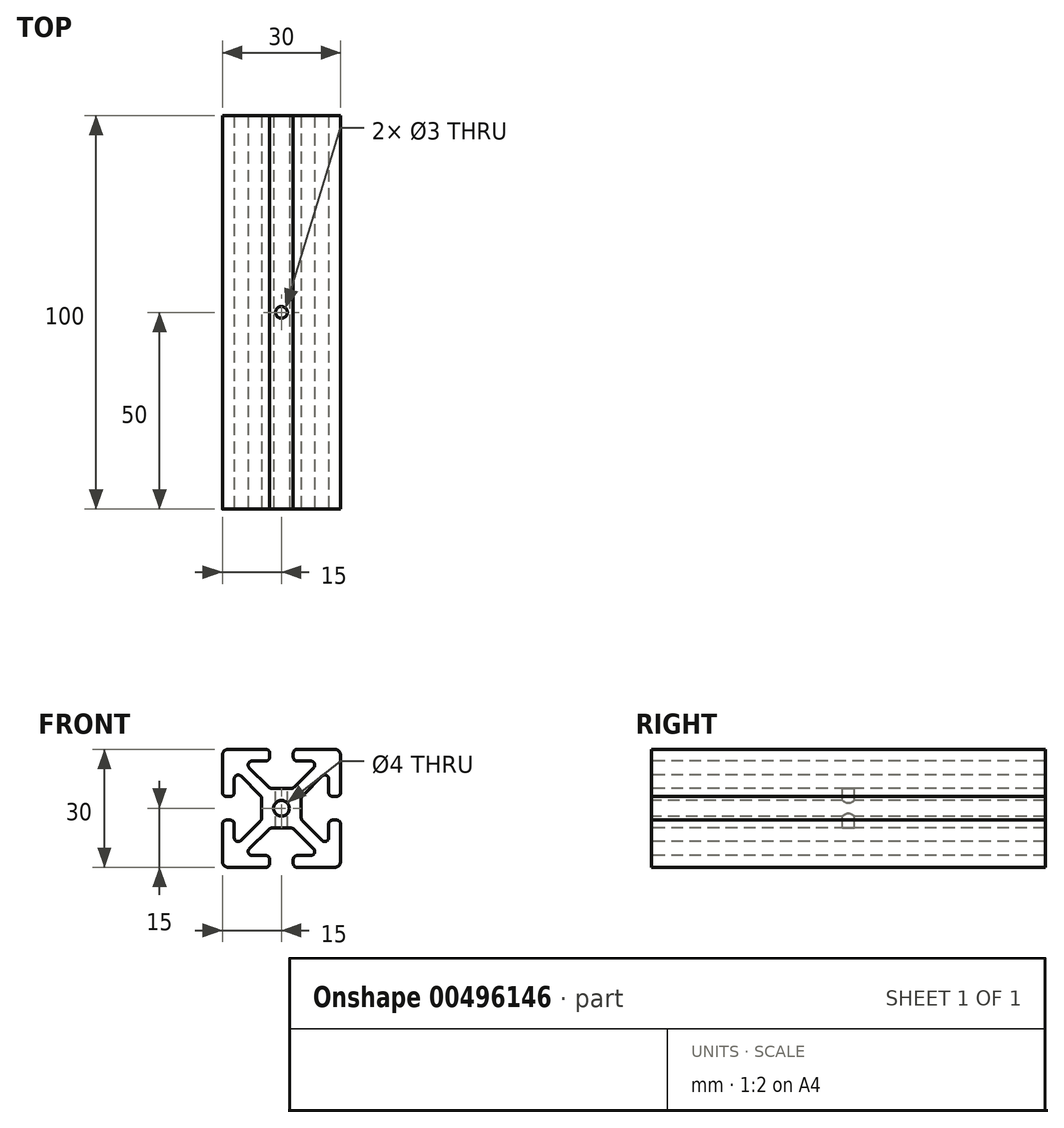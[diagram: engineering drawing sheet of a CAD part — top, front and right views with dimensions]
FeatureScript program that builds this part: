
annotation { "Feature Type Name" : "Feature", "Feature Type Description" : "" }
export const myFeature = defineFeature(function(context is Context, id is Id, definition is map)
    precondition{}
    {
        {
            var Q0;
            Q0=qCreatedBy(makeId("Front.planeOp"),FACE);
            var sketch = newSketch(context, id + "F0", { "sketchPlane" : qUnion([Q0])});
            skLineSegment(sketch, "E0.bottom", {"start": v(13.5, 15) * mm, "end": v(4, 15) * mm});
            skLineSegment(sketch, "E0.top", {"start": v(13.5, -15) * mm, "end": v(4, -15) * mm});
            skLineSegment(sketch, "E0.left", {"start": v(15, 13.5) * mm, "end": v(15, 4) * mm});
            skLineSegment(sketch, "E0.right", {"start": v(-15, 13.5) * mm, "end": v(-15, 4) * mm});
            skPoint(sketch, "E0.middle", {"position": v(0, 0) * mm});
            skLineSegment(sketch, "E1.bottom", {"start": v(7.46, 12) * mm, "end": v(4, 12) * mm});
            skLineSegment(sketch, "E1.top", {"start": v(7.46, -12) * mm, "end": v(4, -12) * mm});
            skLineSegment(sketch, "E1.left", {"start": v(12, 7.46) * mm, "end": v(12, 4) * mm});
            skLineSegment(sketch, "E1.right", {"start": v(-12, 7.46) * mm, "end": v(-12, 4) * mm});
            skLineSegment(sketch, "E2", {"start": v(8.17, 10.3) * mm, "end": v(3.32, 5.44) * mm});
            skLineSegment(sketch, "E3", {"start": v(-8.17, -10.3) * mm, "end": v(-3.32, -5.44) * mm});
            skLineSegment(sketch, "E4", {"start": v(-8.17, 10.3) * mm, "end": v(-3.32, 5.44) * mm});
            skLineSegment(sketch, "E5", {"start": v(-10.3, 8.17) * mm, "end": v(-5.44, 3.32) * mm});
            skPoint(sketch, "E6.orphan", {"position": v(12, 12) * mm});
            skPoint(sketch, "E7.orphan", {"position": v(12, -12) * mm});
            skPoint(sketch, "E8.orphan", {"position": v(-12, -12) * mm});
            skPoint(sketch, "E9.orphan", {"position": v(-12, 12) * mm});
            skLineSegment(sketch, "E10.trimOffspring", {"start": v(-5.44, -3.32) * mm, "end": v(-10.3, -8.17) * mm});
            skLineSegment(sketch, "E11.trimOffspring", {"start": v(5.44, -3.32) * mm, "end": v(10.3, -8.17) * mm});
            skLineSegment(sketch, "E12.trimOffspring", {"start": v(5.44, 3.32) * mm, "end": v(10.3, 8.17) * mm});
            skLineSegment(sketch, "E13.trimOffspring", {"start": v(3.32, -5.44) * mm, "end": v(8.17, -10.3) * mm});
            skLineSegment(sketch, "E14.bottom", {"start": v(2.26, 5) * mm, "end": v(-2.26, 5) * mm});
            skLineSegment(sketch, "E14.top", {"start": v(2.26, -5) * mm, "end": v(-2.26, -5) * mm});
            skLineSegment(sketch, "E14.left", {"start": v(5, 2.26) * mm, "end": v(5, -2.26) * mm});
            skLineSegment(sketch, "E14.right", {"start": v(-5, 2.26) * mm, "end": v(-5, -2.26) * mm});
            skPoint(sketch, "E15.orphan", {"position": v(5, 5) * mm});
            skPoint(sketch, "E16.orphan", {"position": v(5, -5) * mm});
            skPoint(sketch, "E17.orphan", {"position": v(-5, -5) * mm});
            skPoint(sketch, "E18.orphan", {"position": v(-5, 5) * mm});
            skCircle(sketch, "E19", {"center": v(0, 0) * mm, "radius": 2 * mm});
            skLineSegment(sketch, "E20", {"start": v(-3, 14) * mm, "end": v(-3, 13) * mm});
            skLineSegment(sketch, "E21", {"start": v(3, 14) * mm, "end": v(3, 13) * mm});
            skLineSegment(sketch, "E22.trimOffspring", {"start": v(-3, -13) * mm, "end": v(-3, -14) * mm});
            skLineSegment(sketch, "E23.trimOffspring", {"start": v(-4, 12) * mm, "end": v(-7.46, 12) * mm});
            skLineSegment(sketch, "E24.trimOffspring", {"start": v(-4, 15) * mm, "end": v(-13.5, 15) * mm});
            skLineSegment(sketch, "E25.trimOffspring", {"start": v(3, -13) * mm, "end": v(3, -14) * mm});
            skLineSegment(sketch, "E26.trimOffspring", {"start": v(-4, -12) * mm, "end": v(-7.46, -12) * mm});
            skLineSegment(sketch, "E27.trimOffspring", {"start": v(-4, -15) * mm, "end": v(-13.5, -15) * mm});
            skLineSegment(sketch, "E28", {"start": v(-14, 3) * mm, "end": v(-13, 3) * mm});
            skLineSegment(sketch, "E29", {"start": v(-14, -3) * mm, "end": v(-13, -3) * mm});
            skLineSegment(sketch, "E30.trimOffspring", {"start": v(-12, -4) * mm, "end": v(-12, -7.46) * mm});
            skLineSegment(sketch, "E31.trimOffspring", {"start": v(-15, -4) * mm, "end": v(-15, -13.5) * mm});
            skLineSegment(sketch, "E32.trimOffspring", {"start": v(13, 3) * mm, "end": v(14, 3) * mm});
            skLineSegment(sketch, "E33.trimOffspring", {"start": v(13, -3) * mm, "end": v(14, -3) * mm});
            skLineSegment(sketch, "E34.trimOffspring", {"start": v(12, -4) * mm, "end": v(12, -7.46) * mm});
            skLineSegment(sketch, "E35.trimOffspring", {"start": v(15, -4) * mm, "end": v(15, -13.5) * mm});
            skPoint(sketch, "E36.visualSharp", {"position": v(-15, 15) * mm});
            skArc(sketch, "E36.filletArc", {"start": v(-13.5, 15) * mm, "mid": v(-14.56, 14.56) * mm, "end": v(-15, 13.5) * mm});
            skPoint(sketch, "E37.visualSharp", {"position": v(15, 15) * mm});
            skArc(sketch, "E37.filletArc", {"start": v(15, 13.5) * mm, "mid": v(14.56, 14.56) * mm, "end": v(13.5, 15) * mm});
            skPoint(sketch, "E38.visualSharp", {"position": v(15, -15) * mm});
            skArc(sketch, "E38.filletArc", {"start": v(13.5, -15) * mm, "mid": v(14.56, -14.56) * mm, "end": v(15, -13.5) * mm});
            skPoint(sketch, "E39.visualSharp", {"position": v(-15, -15) * mm});
            skArc(sketch, "E39.filletArc", {"start": v(-15, -13.5) * mm, "mid": v(-14.56, -14.56) * mm, "end": v(-13.5, -15) * mm});
            skPoint(sketch, "E40.visualSharp", {"position": v(-5, -2.88) * mm});
            skArc(sketch, "E40.filletArc", {"start": v(-5.44, -3.32) * mm, "mid": v(-5.11, -2.83) * mm, "end": v(-5, -2.26) * mm});
            skPoint(sketch, "E41.visualSharp", {"position": v(-2.88, -5) * mm});
            skArc(sketch, "E41.filletArc", {"start": v(-2.26, -5) * mm, "mid": v(-2.83, -5.11) * mm, "end": v(-3.32, -5.44) * mm});
            skPoint(sketch, "E42.visualSharp", {"position": v(2.88, -5) * mm});
            skArc(sketch, "E42.filletArc", {"start": v(3.32, -5.44) * mm, "mid": v(2.83, -5.11) * mm, "end": v(2.26, -5) * mm});
            skPoint(sketch, "E43.visualSharp", {"position": v(5, -2.88) * mm});
            skArc(sketch, "E43.filletArc", {"start": v(5, -2.26) * mm, "mid": v(5.11, -2.83) * mm, "end": v(5.44, -3.32) * mm});
            skPoint(sketch, "E44.visualSharp", {"position": v(5, 2.88) * mm});
            skArc(sketch, "E44.filletArc", {"start": v(5.44, 3.32) * mm, "mid": v(5.11, 2.83) * mm, "end": v(5, 2.26) * mm});
            skPoint(sketch, "E45.visualSharp", {"position": v(2.88, 5) * mm});
            skArc(sketch, "E45.filletArc", {"start": v(2.26, 5) * mm, "mid": v(2.83, 5.11) * mm, "end": v(3.32, 5.44) * mm});
            skPoint(sketch, "E46.visualSharp", {"position": v(-2.88, 5) * mm});
            skArc(sketch, "E46.filletArc", {"start": v(-3.32, 5.44) * mm, "mid": v(-2.83, 5.11) * mm, "end": v(-2.26, 5) * mm});
            skPoint(sketch, "E47.visualSharp", {"position": v(-3, 12) * mm});
            skArc(sketch, "E47.filletArc", {"start": v(-4, 12) * mm, "mid": v(-3.3, 12.3) * mm, "end": v(-3, 13) * mm});
            skPoint(sketch, "E48.visualSharp", {"position": v(-3, 15) * mm});
            skArc(sketch, "E48.filletArc", {"start": v(-3, 14) * mm, "mid": v(-3.3, 14.7) * mm, "end": v(-4, 15) * mm});
            skPoint(sketch, "E49.visualSharp", {"position": v(3, 15) * mm});
            skArc(sketch, "E49.filletArc", {"start": v(4, 15) * mm, "mid": v(3.3, 14.7) * mm, "end": v(3, 14) * mm});
            skPoint(sketch, "E50.visualSharp", {"position": v(3, 12) * mm});
            skArc(sketch, "E50.filletArc", {"start": v(3, 13) * mm, "mid": v(3.3, 12.3) * mm, "end": v(4, 12) * mm});
            skPoint(sketch, "E51.visualSharp", {"position": v(12, 3) * mm});
            skArc(sketch, "E51.filletArc", {"start": v(12, 4) * mm, "mid": v(12.3, 3.3) * mm, "end": v(13, 3) * mm});
            skPoint(sketch, "E52.visualSharp", {"position": v(15, 3) * mm});
            skArc(sketch, "E52.filletArc", {"start": v(14, 3) * mm, "mid": v(14.7, 3.3) * mm, "end": v(15, 4) * mm});
            skPoint(sketch, "E53.visualSharp", {"position": v(15, -3) * mm});
            skArc(sketch, "E53.filletArc", {"start": v(15, -4) * mm, "mid": v(14.7, -3.3) * mm, "end": v(14, -3) * mm});
            skPoint(sketch, "E54.visualSharp", {"position": v(12, -3) * mm});
            skArc(sketch, "E54.filletArc", {"start": v(13, -3) * mm, "mid": v(12.3, -3.3) * mm, "end": v(12, -4) * mm});
            skPoint(sketch, "E55.visualSharp", {"position": v(3, -12) * mm});
            skArc(sketch, "E55.filletArc", {"start": v(4, -12) * mm, "mid": v(3.3, -12.3) * mm, "end": v(3, -13) * mm});
            skPoint(sketch, "E56.visualSharp", {"position": v(3, -15) * mm});
            skArc(sketch, "E56.filletArc", {"start": v(3, -14) * mm, "mid": v(3.3, -14.7) * mm, "end": v(4, -15) * mm});
            skPoint(sketch, "E57.visualSharp", {"position": v(-3, -12) * mm});
            skArc(sketch, "E57.filletArc", {"start": v(-3, -13) * mm, "mid": v(-3.3, -12.3) * mm, "end": v(-4, -12) * mm});
            skPoint(sketch, "E58.visualSharp", {"position": v(-3, -15) * mm});
            skArc(sketch, "E58.filletArc", {"start": v(-4, -15) * mm, "mid": v(-3.3, -14.7) * mm, "end": v(-3, -14) * mm});
            skPoint(sketch, "E59.visualSharp", {"position": v(-12, -3) * mm});
            skArc(sketch, "E59.filletArc", {"start": v(-12, -4) * mm, "mid": v(-12.3, -3.3) * mm, "end": v(-13, -3) * mm});
            skPoint(sketch, "E60.visualSharp", {"position": v(-15, -3) * mm});
            skArc(sketch, "E60.filletArc", {"start": v(-14, -3) * mm, "mid": v(-14.7, -3.3) * mm, "end": v(-15, -4) * mm});
            skPoint(sketch, "E61.visualSharp", {"position": v(-15, 3) * mm});
            skArc(sketch, "E61.filletArc", {"start": v(-15, 4) * mm, "mid": v(-14.7, 3.3) * mm, "end": v(-14, 3) * mm});
            skPoint(sketch, "E62.visualSharp", {"position": v(-12, 3) * mm});
            skArc(sketch, "E62.filletArc", {"start": v(-13, 3) * mm, "mid": v(-12.3, 3.3) * mm, "end": v(-12, 4) * mm});
            skPoint(sketch, "E63.visualSharp", {"position": v(9.88, 12) * mm});
            skArc(sketch, "E63.filletArc", {"start": v(8.17, 10.3) * mm, "mid": v(8.39, 11.38) * mm, "end": v(7.46, 12) * mm});
            skPoint(sketch, "E64.visualSharp", {"position": v(12, 9.88) * mm});
            skArc(sketch, "E64.filletArc", {"start": v(12, 7.46) * mm, "mid": v(11.38, 8.39) * mm, "end": v(10.3, 8.17) * mm});
            skPoint(sketch, "E65.visualSharp", {"position": v(12, -9.88) * mm});
            skArc(sketch, "E65.filletArc", {"start": v(10.3, -8.17) * mm, "mid": v(11.38, -8.39) * mm, "end": v(12, -7.46) * mm});
            skPoint(sketch, "E66.visualSharp", {"position": v(9.88, -12) * mm});
            skArc(sketch, "E66.filletArc", {"start": v(7.46, -12) * mm, "mid": v(8.39, -11.38) * mm, "end": v(8.17, -10.3) * mm});
            skPoint(sketch, "E67.visualSharp", {"position": v(-12, -9.88) * mm});
            skArc(sketch, "E67.filletArc", {"start": v(-12, -7.46) * mm, "mid": v(-11.38, -8.39) * mm, "end": v(-10.3, -8.17) * mm});
            skPoint(sketch, "E68.visualSharp", {"position": v(-9.88, -12) * mm});
            skArc(sketch, "E68.filletArc", {"start": v(-8.17, -10.3) * mm, "mid": v(-8.39, -11.38) * mm, "end": v(-7.46, -12) * mm});
            skPoint(sketch, "E69.visualSharp", {"position": v(-12, 9.88) * mm});
            skArc(sketch, "E69.filletArc", {"start": v(-10.3, 8.17) * mm, "mid": v(-11.38, 8.39) * mm, "end": v(-12, 7.46) * mm});
            skPoint(sketch, "E70.visualSharp", {"position": v(-9.88, 12) * mm});
            skArc(sketch, "E70.filletArc", {"start": v(-7.46, 12) * mm, "mid": v(-8.39, 11.38) * mm, "end": v(-8.17, 10.3) * mm});
            skPoint(sketch, "E71.visualSharp", {"position": v(-5, 2.88) * mm});
            skArc(sketch, "E71.filletArc", {"start": v(-5, 2.26) * mm, "mid": v(-5.11, 2.83) * mm, "end": v(-5.44, 3.32) * mm});
            skSolve(sketch);
        }
        {
            var Q0;
            Q0=qSketchRegion(id+"F0",true);
            extrude(context, id + "F1", {"entities" : qUnion([Q0]), "oppositeDirection" : true, "depth" : 100 * mm});
        }
        {
            var Q0;
            Q0=makeQuery(id+"F1.opExtrude","SWEPT_FACE",FACE,{"disambiguationData":[OSD([sQuery(id+"F0.wireOp",EDGE,"E14.bottom")])]});
            var sketch = newSketch(context, id + "F2", { "sketchPlane" : qUnion([Q0])});
            skCircle(sketch, "E72", {"center": v(0, 50) * mm, "radius": 1.5 * mm});
            skPoint(sketch, "E72.centerSnap0", {"position": v(0, 100) * mm});
            skPoint(sketch, "E72.centerSnap1", {"position": v(2.26, 50) * mm});
            skSolve(sketch);
        }
        {
            var Q0;
            Q0 = qSketchRegion(id + "F2", true);
            extrude(context, id + "F3", {"entities" : qUnion([Q0]), "operationType" : NewBodyOperationType.REMOVE, "oppositeDirection" : true, "depth" : 10 * mm});
        }
    });
